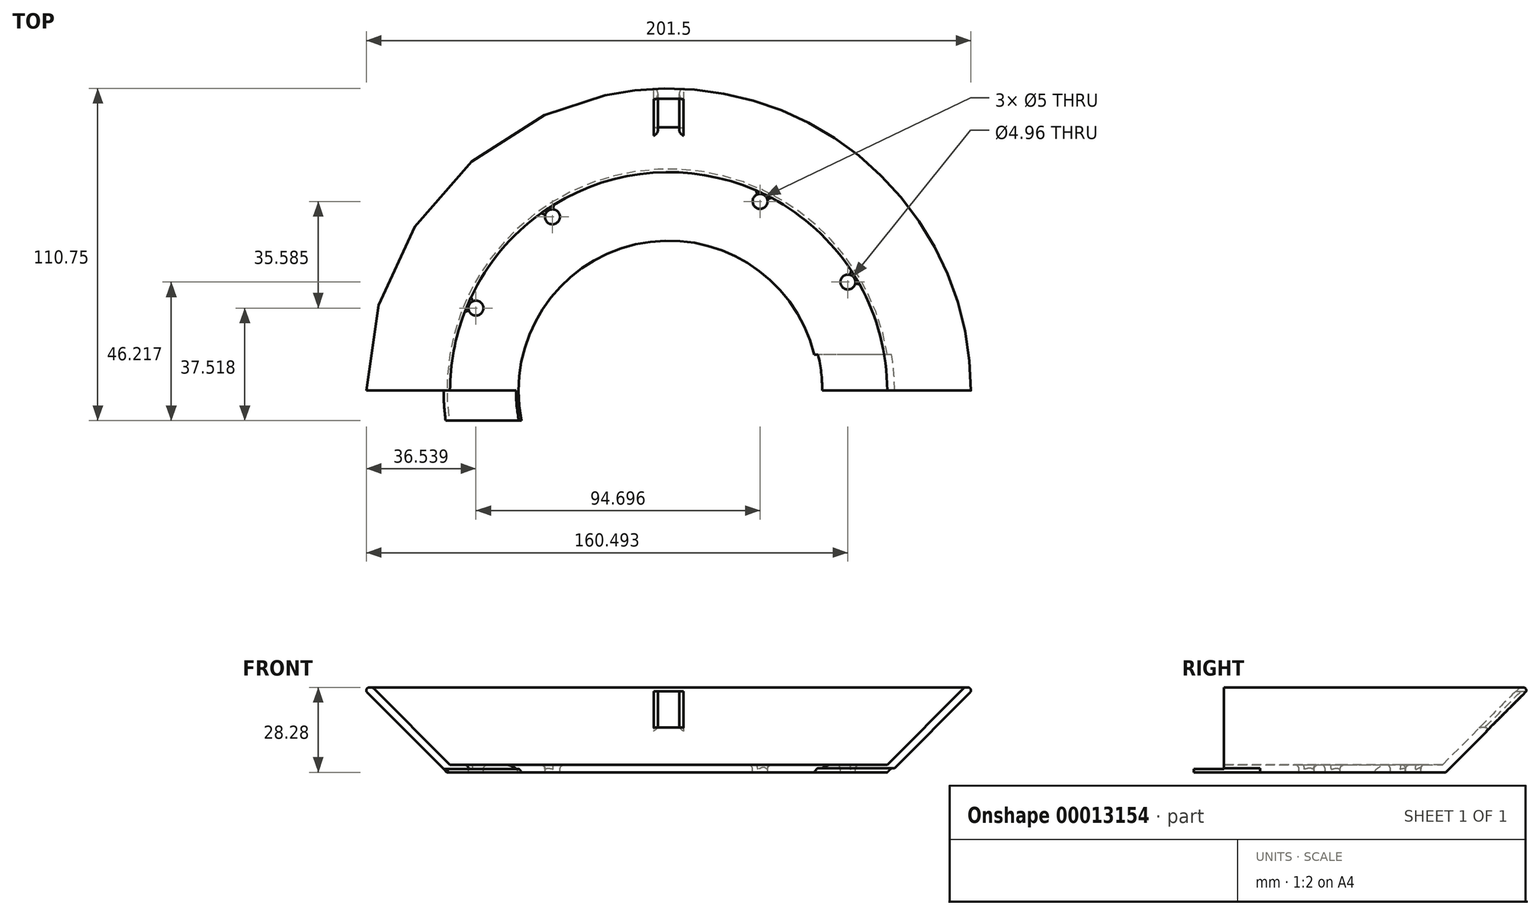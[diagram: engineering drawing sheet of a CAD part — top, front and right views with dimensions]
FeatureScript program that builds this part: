
annotation { "Feature Type Name" : "Feature", "Feature Type Description" : "" }
export const myFeature = defineFeature(function(context is Context, id is Id, definition is map)
    precondition{}
    {
        {
            var Q0;
            Q0=qCreatedBy(makeId("Top.planeOp"),FACE);
            var sketch = newSketch(context, id + "F0", { "sketchPlane" : qUnion([Q0])});
            skCircle(sketch, "E0", {"center": v(0, 0) * mm, "radius": 74 * mm});
            skSolve(sketch);
        }
        {
            var Q0;
            Q0=qCreatedBy(makeId("Top.planeOp"),FACE);
            var sketch = newSketch(context, id + "F1", { "sketchPlane" : qUnion([Q0])});
            skCircle(sketch, "E1", {"center": v(0, 0) * mm, "radius": 50 * mm});
            skSolve(sketch);
        }
        {
            var Q0;
            Q0=qCreatedBy(makeId("Top.planeOp"),FACE);
            var sketch = newSketch(context, id + "F2", { "sketchPlane" : qUnion([Q0])});
            skCircle(sketch, "E2", {"center": v(0, 0) * mm, "radius": 74 * mm});
            skSolve(sketch);
        }
        {
            var Q0;
            Q0=qCreatedBy(makeId("Top.planeOp"),FACE);
            var sketch = newSketch(context, id + "F3", { "sketchPlane" : qUnion([Q0])});
            skCircle(sketch, "E3", {"center": v(0, 0) * mm, "radius": 71.5 * mm});
            skSolve(sketch);
        }
        {
            var Q0;
            Q0=qCreatedBy(makeId("Front.planeOp"),FACE);
            var sketch = newSketch(context, id + "F4", { "sketchPlane" : qUnion([Q0])});
            skLineSegment(sketch, "E4", {"start": v(0, 0) * mm, "end": v(0, 40.4) * mm});
            skSolve(sketch);
        }
        {
            var Q0;
            Q0=qCreatedBy(makeId("Front.planeOp"),FACE);
            var sketch = newSketch(context, id + "F5", { "sketchPlane" : qUnion([Q0])});
            skLineSegment(sketch, "E5", {"start": v(-73.88, 0) * mm, "end": v(-73.88, 17.5) * mm});
            skSolve(sketch);
        }
        {
            var Q0;
            Q0=qCreatedBy(makeId("Front.planeOp"),FACE);
            var sketch = newSketch(context, id + "F6", { "sketchPlane" : qUnion([Q0])});
            skLineSegment(sketch, "E6", {"start": v(0, 0) * mm, "end": v(-73.88, 0) * mm});
            skLineSegment(sketch, "E7", {"start": v(-73.88, 0) * mm, "end": v(-102.16, 28.28) * mm});
            skLineSegment(sketch, "E8", {"start": v(-102.16, 28.28) * mm, "end": v(-98.63, 28.28) * mm});
            skLineSegment(sketch, "E9", {"start": v(-98.63, 28.28) * mm, "end": v(-72.84, 2.5) * mm});
            skLineSegment(sketch, "E10", {"start": v(-72.84, 2.5) * mm, "end": v(0, 2.5) * mm});
            skLineSegment(sketch, "E11", {"start": v(0, 2.5) * mm, "end": v(0, 0) * mm});
            skSolve(sketch);
        }
        {
            var Q0;
            Q0 = qSketchRegion(id + "F6", true);
            var Q1;
            Q1=sQuery(id+"F4.wireOp",EDGE,"E4");
            revolve(context, id + "F7", {"entities" : qUnion([Q0]), "axis" : qUnion([Q1]), "revolveType" : RevolveType.FULL});
        }
        {
            var Q0;
            Q0 = qSketchRegion(id + "F1", true);
            var Q1;
            Q1=makeQuery(id+"Fg0lEvoKYzCflzx_0.opExtrude","CAP_FACE",FACE,{"disambiguationData":[OSD([sQuery(id+"F0.wireOp",EDGE,"E0")])],"isStart":false});
            var Q2;
            Q2=makeQuery(id+"Fg0lEvoKYzCflzx_0.opExtrude","CAP_FACE",FACE,{"disambiguationData":[OSD([sQuery(id+"F0.wireOp",EDGE,"E0")])],"isStart":false});
            var Q3;
            Q3=makeQuery(id+"Fg0lEvoKYzCflzx_0.opExtrude","SWEPT_BODY",BODY,{"disambiguationData":[OSD([sQuery(id+"F0.wireOp",EDGE,"E0")])]});
            extrude(context, id + "F8", {"entities" : qUnion([Q0]), "operationType" : NewBodyOperationType.REMOVE, "endBoundEntityFace" : qUnion([Q1]), "depth" : 10 * mm, "hasSecondDirection" : true, "secondDirectionOppositeDirection" : true, "secondDirectionBoundEntityFace" : qUnion([Q2]), "secondDirectionBoundEntityBody" : qUnion([Q3]), "secondDirectionDepth" : 2 * mm});
        }
        {
            var Q0;
            Q0=qCreatedBy(makeId("Top.planeOp"),FACE);
            var sketch = newSketch(context, id + "F9", { "sketchPlane" : qUnion([Q0])});
            skLineSegment(sketch, "E12.bottom", {"start": v(-112.29, -107.04) * mm, "end": v(0, -107.04) * mm});
            skLineSegment(sketch, "E12.top", {"start": v(-112.29, 0) * mm, "end": v(0, 0) * mm});
            skLineSegment(sketch, "E12.left", {"start": v(-112.29, -107.04) * mm, "end": v(-112.29, 0) * mm});
            skLineSegment(sketch, "E12.right", {"start": v(0, -107.04) * mm, "end": v(0, 0) * mm});
            skSolve(sketch);
        }
        {
            var Q0;
            Q0 = qSketchRegion(id + "F9", true);
            extrude(context, id + "F10", {"entities" : qUnion([Q0]), "operationType" : NewBodyOperationType.REMOVE, "depth" : 35.83 * mm, "hasSecondDirection" : true, "secondDirectionOppositeDirection" : false, "secondDirectionDepth" : 1.1 * mm});
        }
        {
            var Q0;
            Q0=qCreatedBy(makeId("Top.planeOp"),FACE);
            var sketch = newSketch(context, id + "F11", { "sketchPlane" : qUnion([Q0])});
            skLineSegment(sketch, "E13.bottom", {"start": v(-110.56, -110) * mm, "end": v(0, -110) * mm});
            skLineSegment(sketch, "E13.top", {"start": v(-110.56, -10) * mm, "end": v(0, -10) * mm});
            skLineSegment(sketch, "E13.left", {"start": v(-110.56, -110) * mm, "end": v(-110.56, -10) * mm});
            skLineSegment(sketch, "E13.right", {"start": v(0, -110) * mm, "end": v(0, -10) * mm});
            skSolve(sketch);
        }
        {
            var Q0;
            Q0 = qSketchRegion(id + "F11", true);
            extrude(context, id + "F12", {"entities" : qUnion([Q0]), "operationType" : NewBodyOperationType.REMOVE, "depth" : 59.24 * mm, "hasSecondDirection" : true, "secondDirectionOppositeDirection" : true, "secondDirectionDepth" : 14.7 * mm});
        }
        {
            var Q0;
            Q0=qCreatedBy(makeId("Top.planeOp"),FACE);
            var sketch = newSketch(context, id + "F13", { "sketchPlane" : qUnion([Q0])});
            skLineSegment(sketch, "E14.bottom", {"start": v(0, -106.93) * mm, "end": v(105.7, -106.93) * mm});
            skLineSegment(sketch, "E14.top", {"start": v(0, 0) * mm, "end": v(105.7, 0) * mm});
            skLineSegment(sketch, "E14.left", {"start": v(0, -106.93) * mm, "end": v(0, 0) * mm});
            skLineSegment(sketch, "E14.right", {"start": v(105.7, -106.93) * mm, "end": v(105.7, 0) * mm});
            skSolve(sketch);
        }
        {
            var Q0;
            Q0=makeQuery(id+"F13.imprint","IMPRINT",FACE,{"disambiguationData":[TD([[makeQuery(id+"F13.imprint","IMPRINT",EDGE,{"derivedFrom":sQuery(id+"F13.wireOp",EDGE,"E14.bottom")}),1.0]])]});
            extrude(context, id + "F14", {"entities" : qUnion([Q0]), "operationType" : NewBodyOperationType.REMOVE, "depth" : 41.75 * mm, "hasSecondDirection" : true, "secondDirectionOppositeDirection" : true, "secondDirectionDepth" : 25 * mm});
        }
        {
            var Q0;
            Q0=qCreatedBy(makeId("Top.planeOp"),FACE);
            var sketch = newSketch(context, id + "F15", { "sketchPlane" : qUnion([Q0])});
            skLineSegment(sketch, "E15.bottom", {"start": v(92.46, 0) * mm, "end": v(32.15, 0) * mm});
            skLineSegment(sketch, "E15.top", {"start": v(92.46, 12) * mm, "end": v(32.15, 12) * mm});
            skLineSegment(sketch, "E15.left", {"start": v(92.46, 0) * mm, "end": v(92.46, 12) * mm});
            skLineSegment(sketch, "E15.right", {"start": v(32.15, 0) * mm, "end": v(32.15, 12) * mm});
            skSolve(sketch);
        }
        {
            var Q0;
            Q0 = qSketchRegion(id + "F15", true);
            extrude(context, id + "F16", {"entities" : qUnion([Q0]), "operationType" : NewBodyOperationType.REMOVE, "depth" : (2.5 - 1.1) * mm});
        }
        {
            var Q0;
            Q0=qCreatedBy(makeId("Top.planeOp"),FACE);
            var sketch = newSketch(context, id + "F17", { "sketchPlane" : qUnion([Q0])});
            skCircle(sketch, "E16", {"center": v(30.48, 63.1) * mm, "radius": 2.5 * mm});
            skCircle(sketch, "E17", {"center": v(59.74, 36.22) * mm, "radius": 2.48 * mm});
            skCircle(sketch, "E18", {"center": v(-38.7, 57.96) * mm, "radius": 2.5 * mm});
            skCircle(sketch, "E19", {"center": v(-64.21, 27.52) * mm, "radius": 2.5 * mm});
            skLineSegment(sketch, "E20", {"start": v(0, 0) * mm, "end": v(-25.66, 0) * mm});
            skSolve(sketch);
        }
        {
            var Q0;
            Q0 = qSketchRegion(id + "F17", true);
            extrude(context, id + "F18", {"entities" : qUnion([Q0]), "operationType" : NewBodyOperationType.REMOVE, "oppositeDirection" : true, "depth" : 25 * mm, "hasSecondDirection" : true, "secondDirectionOppositeDirection" : false, "secondDirectionDepth" : 25 * mm});
        }
        {
            var Q0;
            Q0=makeQuery(id+"F7.opRevolve","SWEPT_EDGE",EDGE,{"disambiguationData":[OSD([sQuery(id+"F6.wireOp",EDGE,"E7"),sQuery(id+"F6.wireOp",EDGE,"E8")])]});
            var Q1;
            Q1=makeQuery(id+"F7.opRevolve","SWEPT_EDGE",EDGE,{"disambiguationData":[OSD([sQuery(id+"F6.wireOp",EDGE,"E8"),sQuery(id+"F6.wireOp",EDGE,"E9")])]});
            fillet(context, id + "F19", {"entities" : qUnion([Q0, Q1]), "radius" : 1 * mm, "tangentPropagation" : true, "allowEdgeOverflow" : false});
        }
        {
            var Q0;
            Q0=makeQuery(id+"F18.boolean.opBoolean","INTERSECT",EDGE,{"derivedFrom":[makeQuery(id+"F7.opRevolve","SWEPT_FACE",FACE,{"disambiguationData":[OSD([sQuery(id+"F6.wireOp",EDGE,"E10")])]}),makeQuery(id+"F18.opExtrude","SWEPT_FACE",FACE,{"disambiguationData":[OSD([sQuery(id+"F17.wireOp",EDGE,"E19")])]})]});
            var Q1;
            Q1=makeQuery(id+"F18.boolean.opBoolean","INTERSECT",EDGE,{"derivedFrom":[makeQuery(id+"F7.opRevolve","SWEPT_FACE",FACE,{"disambiguationData":[OSD([sQuery(id+"F6.wireOp",EDGE,"E10")])]}),makeQuery(id+"F18.opExtrude","SWEPT_FACE",FACE,{"disambiguationData":[OSD([sQuery(id+"F17.wireOp",EDGE,"E18")])]})]});
            var Q2;
            Q2=makeQuery(id+"F18.boolean.opBoolean","INTERSECT",EDGE,{"derivedFrom":[makeQuery(id+"F7.opRevolve","SWEPT_FACE",FACE,{"disambiguationData":[OSD([sQuery(id+"F6.wireOp",EDGE,"E10")])]}),makeQuery(id+"F18.opExtrude","SWEPT_FACE",FACE,{"disambiguationData":[OSD([sQuery(id+"F17.wireOp",EDGE,"E16")])]})]});
            var Q3;
            Q3=makeQuery(id+"F18.boolean.opBoolean","INTERSECT",EDGE,{"derivedFrom":[makeQuery(id+"F7.opRevolve","SWEPT_FACE",FACE,{"disambiguationData":[OSD([sQuery(id+"F6.wireOp",EDGE,"E10")])]}),makeQuery(id+"F18.opExtrude","SWEPT_FACE",FACE,{"disambiguationData":[OSD([sQuery(id+"F17.wireOp",EDGE,"E17")])]})]});
            fillet(context, id + "F20", {"entities" : qUnion([Q0, Q1, Q2, Q3]), "radius" : 1.5 * mm, "tangentPropagation" : true, "allowEdgeOverflow" : false});
        }
        {
            var Q0;
            Q0=qCreatedBy(makeId("Top.planeOp"),FACE);
            var sketch = newSketch(context, id + "F21", { "sketchPlane" : qUnion([Q0])});
            skLineSegment(sketch, "E21.rect.bottom", {"start": v(-3.5, 74) * mm, "end": v(3.5, 74) * mm});
            skLineSegment(sketch, "E21.rect.top", {"start": v(-3.5, 101) * mm, "end": v(3.5, 101) * mm});
            skLineSegment(sketch, "E21.rect.left", {"start": v(-3.5, 74) * mm, "end": v(-3.5, 101) * mm});
            skLineSegment(sketch, "E21.rect.right", {"start": v(3.5, 74) * mm, "end": v(3.5, 101) * mm});
            skPoint(sketch, "E21.rect.middle", {"position": v(0, 87.5) * mm});
            skSolve(sketch);
        }
        {
            var Q0;
            Q0 = qSketchRegion(id + "F21", true);
            extrude(context, id + "F22", {"entities" : qUnion([Q0]), "operationType" : NewBodyOperationType.REMOVE, "depth" : 27 * mm, "hasSecondDirection" : true, "secondDirectionOppositeDirection" : false, "secondDirectionDepth" : 15 * mm});
        }
        {
            var Q0;
            Q0=makeQuery(id+"F22.boolean.opBoolean","INTERSECT",EDGE,{"derivedFrom":[makeQuery(id+"F7.opRevolve","SWEPT_FACE",FACE,{"disambiguationData":[OSD([sQuery(id+"F6.wireOp",EDGE,"E9")])]}),makeQuery(id+"F22.opExtrude","SWEPT_FACE",FACE,{"disambiguationData":[OSD([sQuery(id+"F21.wireOp",EDGE,"E21.rect.left")])]})]});
            var Q1;
            Q1=makeQuery(id+"F22.boolean.opBoolean","INTERSECT",EDGE,{"derivedFrom":[makeQuery(id+"F7.opRevolve","SWEPT_FACE",FACE,{"disambiguationData":[OSD([sQuery(id+"F6.wireOp",EDGE,"E7")])]}),makeQuery(id+"F22.opExtrude","SWEPT_FACE",FACE,{"disambiguationData":[OSD([sQuery(id+"F21.wireOp",EDGE,"E21.rect.left")])]})]});
            var Q2;
            Q2=makeQuery(id+"F22.boolean.opBoolean","INTERSECT",EDGE,{"derivedFrom":[makeQuery(id+"F7.opRevolve","SWEPT_FACE",FACE,{"disambiguationData":[OSD([sQuery(id+"F6.wireOp",EDGE,"E9")])]}),makeQuery(id+"F22.opExtrude","SWEPT_FACE",FACE,{"disambiguationData":[OSD([sQuery(id+"F21.wireOp",EDGE,"E21.rect.right")])]})]});
            var Q3;
            Q3=makeQuery(id+"F22.boolean.opBoolean","INTERSECT",EDGE,{"derivedFrom":[makeQuery(id+"F7.opRevolve","SWEPT_FACE",FACE,{"disambiguationData":[OSD([sQuery(id+"F6.wireOp",EDGE,"E7")])]}),makeQuery(id+"F22.opExtrude","SWEPT_FACE",FACE,{"disambiguationData":[OSD([sQuery(id+"F21.wireOp",EDGE,"E21.rect.right")])]})]});
            fillet(context, id + "F23", {"entities" : qUnion([Q0, Q1, Q2, Q3]), "radius" : 1.5 * mm, "tangentPropagation" : true, "allowEdgeOverflow" : false});
        }
        {
            var Q0;
            Q0=makeQuery(id+"F22.boolean.opBoolean","INTERSECT",EDGE,{"derivedFrom":[makeQuery(id+"F7.opRevolve","SWEPT_FACE",FACE,{"disambiguationData":[OSD([sQuery(id+"F6.wireOp",EDGE,"E7")])]}),makeQuery(id+"F22.opExtrude","CAP_FACE",FACE,{"disambiguationData":[OSD([sQuery(id+"F21.wireOp",EDGE,"E21.rect.bottom"),sQuery(id+"F21.wireOp",EDGE,"E21.rect.top"),sQuery(id+"F21.wireOp",EDGE,"E21.rect.left"),sQuery(id+"F21.wireOp",EDGE,"E21.rect.right")])],"isStart":true})]});
            var Q1;
            Q1=makeQuery(id+"F22.boolean.opBoolean","INTERSECT",EDGE,{"derivedFrom":[makeQuery(id+"F7.opRevolve","SWEPT_FACE",FACE,{"disambiguationData":[OSD([sQuery(id+"F6.wireOp",EDGE,"E9")])]}),makeQuery(id+"F22.opExtrude","CAP_FACE",FACE,{"disambiguationData":[OSD([sQuery(id+"F21.wireOp",EDGE,"E21.rect.bottom"),sQuery(id+"F21.wireOp",EDGE,"E21.rect.top"),sQuery(id+"F21.wireOp",EDGE,"E21.rect.left"),sQuery(id+"F21.wireOp",EDGE,"E21.rect.right")])],"isStart":true})]});
            fillet(context, id + "F24", {"entities" : qUnion([Q0, Q1]), "radius" : 0.75 * mm, "tangentPropagation" : true, "allowEdgeOverflow" : false});
        }
        {
            var Q0;
            Q0=makeQuery(id+"F8.boolean.opBoolean","INTERSECT",EDGE,{"derivedFrom":[makeQuery(id+"F7.opRevolve","SWEPT_FACE",FACE,{"disambiguationData":[OSD([sQuery(id+"F6.wireOp",EDGE,"E10")])]}),makeQuery(id+"F8.opExtrude","SWEPT_FACE",FACE,{"disambiguationData":[OSD([sQuery(id+"F1.wireOp",EDGE,"E1")])]})]});
            fillet(context, id + "F25", {"entities" : qUnion([Q0]), "radius" : 5 * mm, "tangentPropagation" : true, "allowEdgeOverflow" : false});
        }
    });
